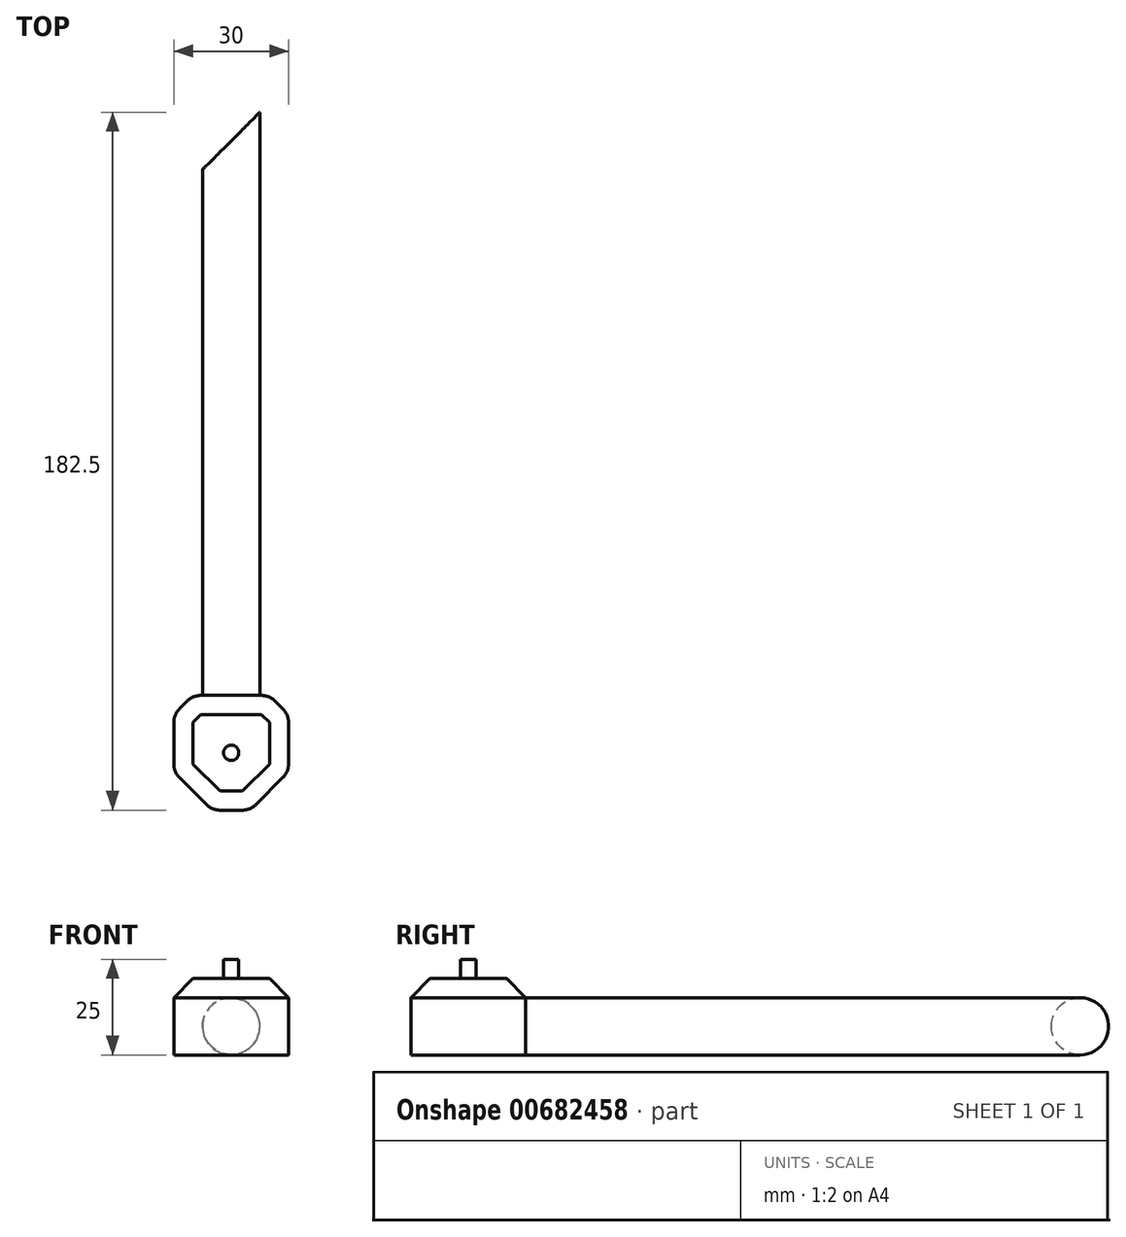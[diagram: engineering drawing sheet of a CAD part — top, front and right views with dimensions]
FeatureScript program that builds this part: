
annotation { "Feature Type Name" : "Feature", "Feature Type Description" : "" }
export const myFeature = defineFeature(function(context is Context, id is Id, definition is map)
    precondition{}
    {
        {
            var Q0;
            Q0=qCreatedBy(makeId("Top.planeOp"),FACE);
            var sketch = newSketch(context, id + "F0", { "sketchPlane" : qUnion([Q0])});
            skLineSegment(sketch, "E0", {"start": v(0, 12.5) * mm, "end": v(0, 150) * mm});
            skLineSegment(sketch, "E1", {"start": v(0, 150) * mm, "end": v(15, 165) * mm});
            skLineSegment(sketch, "E2", {"start": v(15, 165) * mm, "end": v(15, 12.5) * mm});
            skLineSegment(sketch, "E3", {"start": v(12.5, 0) * mm, "end": v(12.5, 0) * mm});
            skLineSegment(sketch, "E4", {"start": v(43.36, 205.51) * mm, "end": v(-124.44, 37.72) * mm, "construction": true});
            skPoint(sketch, "E5.visualSharp", {"position": v(15, 0) * mm});
            skPoint(sketch, "E6.visualSharp", {"position": v(0, 0) * mm});
            skLineSegment(sketch, "E7", {"start": v(15, 12.5) * mm, "end": v(0, 12.5) * mm});
            skSolve(sketch);
        }
        {
            var Q0;
            Q0=makeQuery(id+"F0.imprint","IMPRINT",FACE,{"disambiguationData":[TD([[makeQuery(id+"F0.imprint","IMPRINT",EDGE,{"derivedFrom":sQuery(id+"F0.wireOp",EDGE,"E0")}),-1.0]])]});
            extrude(context, id + "F1", {"entities" : qUnion([Q0]), "depth" : 15 * mm, "offsetDistance" : 25 * mm});
        }
        {
            var Q0;
            Q0=makeQuery(id+"F1.opExtrude","CAP_EDGE",EDGE,{"disambiguationData":[OSD([sQuery(id+"F0.wireOp",EDGE,"E2")])],"isStart":false});
            var Q1;
            Q1=makeQuery(id+"F1.opExtrude","CAP_EDGE",EDGE,{"disambiguationData":[OSD([sQuery(id+"F0.wireOp",EDGE,"E0")])],"isStart":false});
            var Q2;
            Q2=makeQuery(id+"F1.opExtrude","CAP_EDGE",EDGE,{"disambiguationData":[OSD([sQuery(id+"F0.wireOp",EDGE,"E0")])],"isStart":true});
            var Q3;
            Q3=makeQuery(id+"F1.opExtrude","CAP_EDGE",EDGE,{"disambiguationData":[OSD([sQuery(id+"F0.wireOp",EDGE,"E2")])],"isStart":true});
            fillet(context, id + "F2", {"entities" : qUnion([Q0, Q1, Q2, Q3]), "radius" : 7.5 * mm, "tangentPropagation" : true, "allowEdgeOverflow" : false});
        }
        {
            var Q0;
            Q0=qCreatedBy(makeId("Top.planeOp"),FACE);
            var sketch = newSketch(context, id + "F3", { "sketchPlane" : qUnion([Q0])});
            skLineSegment(sketch, "E8.bottom", {"start": v(22.5, 12.5) * mm, "end": v(-7.5, 12.5) * mm});
            skLineSegment(sketch, "E8.top", {"start": v(22.5, -17.5) * mm, "end": v(-7.5, -17.5) * mm});
            skLineSegment(sketch, "E8.left", {"start": v(22.5, 12.5) * mm, "end": v(22.5, -17.5) * mm});
            skLineSegment(sketch, "E8.right", {"start": v(-7.5, 12.5) * mm, "end": v(-7.5, -17.5) * mm});
            skSolve(sketch);
        }
        {
            var Q0;
            Q0 = qSketchRegion(id + "F3", true);
            extrude(context, id + "F4", {"entities" : qUnion([Q0]), "operationType" : NewBodyOperationType.ADD, "depth" : 20 * mm, "offsetDistance" : 25 * mm});
        }
        {
            var Q0;
            Q0=makeQuery(id+"F4.opExtrude","SWEPT_EDGE",EDGE,{"disambiguationData":[OSD([sQuery(id+"F3.wireOp",EDGE,"E8.top"),sQuery(id+"F3.wireOp",EDGE,"E8.right")])]});
            var Q1;
            Q1=makeQuery(id+"F4.opExtrude","SWEPT_EDGE",EDGE,{"disambiguationData":[OSD([sQuery(id+"F3.wireOp",EDGE,"E8.top"),sQuery(id+"F3.wireOp",EDGE,"E8.left")])]});
            chamfer(context, id + "F5", {"entities" : qUnion([Q0, Q1]), "width" : 10 * mm, "tangentPropagation" : true});
        }
        {
            var Q0;
            Q0=makeQuery(id+"F4.opExtrude","SWEPT_EDGE",EDGE,{"disambiguationData":[OSD([sQuery(id+"F3.wireOp",EDGE,"E8.bottom"),sQuery(id+"F3.wireOp",EDGE,"E8.left")])]});
            var Q1;
            Q1=makeQuery(id+"F4.opExtrude","SWEPT_EDGE",EDGE,{"disambiguationData":[OSD([sQuery(id+"F3.wireOp",EDGE,"E8.bottom"),sQuery(id+"F3.wireOp",EDGE,"E8.right")])]});
            chamfer(context, id + "F6", {"entities" : qUnion([Q0, Q1]), "width" : 5 * mm, "tangentPropagation" : true});
        }
        {
            var Q0;
            {var subQ0=sQuery(id+"F3.wireOp",EDGE,"E8.top");Q0=makeQuery(id+"F5.opChamfer","BLEND_EDGE",EDGE,{"blendedFrom":[makeQuery(id+"F4.opExtrude","SWEPT_EDGE",EDGE,{"disambiguationData":[OSD([subQ0,sQuery(id+"F3.wireOp",EDGE,"E8.left")])]}),makeQuery(id+"F4.opExtrude","SWEPT_FACE",FACE,{"disambiguationData":[OSD([subQ0])]})],"blendedInto":[makeQuery(id+"F4.opExtrude","SWEPT_FACE",FACE,{"disambiguationData":[OSD([subQ0])]})]});}
            var Q1;
            {var subQ0=sQuery(id+"F3.wireOp",EDGE,"E8.top");Q1=makeQuery(id+"F5.opChamfer","BLEND_EDGE",EDGE,{"blendedFrom":[makeQuery(id+"F4.opExtrude","SWEPT_EDGE",EDGE,{"disambiguationData":[OSD([subQ0,sQuery(id+"F3.wireOp",EDGE,"E8.right")])]}),makeQuery(id+"F4.opExtrude","SWEPT_FACE",FACE,{"disambiguationData":[OSD([subQ0])]})],"blendedInto":[makeQuery(id+"F4.opExtrude","SWEPT_FACE",FACE,{"disambiguationData":[OSD([subQ0])]})]});}
            var Q2;
            {var subQ0=sQuery(id+"F3.wireOp",EDGE,"E8.right");Q2=makeQuery(id+"F5.opChamfer","BLEND_EDGE",EDGE,{"blendedFrom":[makeQuery(id+"F4.opExtrude","SWEPT_EDGE",EDGE,{"disambiguationData":[OSD([sQuery(id+"F3.wireOp",EDGE,"E8.top"),subQ0])]}),makeQuery(id+"F4.opExtrude","SWEPT_FACE",FACE,{"disambiguationData":[OSD([subQ0])]})],"blendedInto":[makeQuery(id+"F4.opExtrude","SWEPT_FACE",FACE,{"disambiguationData":[OSD([subQ0])]})]});}
            var Q3;
            {var subQ0=sQuery(id+"F3.wireOp",EDGE,"E8.left");Q3=makeQuery(id+"F5.opChamfer","BLEND_EDGE",EDGE,{"blendedFrom":[makeQuery(id+"F4.opExtrude","SWEPT_EDGE",EDGE,{"disambiguationData":[OSD([sQuery(id+"F3.wireOp",EDGE,"E8.top"),subQ0])]}),makeQuery(id+"F4.opExtrude","SWEPT_FACE",FACE,{"disambiguationData":[OSD([subQ0])]})],"blendedInto":[makeQuery(id+"F4.opExtrude","SWEPT_FACE",FACE,{"disambiguationData":[OSD([subQ0])]})]});}
            var Q4;
            {var subQ0=sQuery(id+"F3.wireOp",EDGE,"E8.left");Q4=makeQuery(id+"F6.opChamfer","BLEND_EDGE",EDGE,{"blendedFrom":[makeQuery(id+"F4.opExtrude","SWEPT_EDGE",EDGE,{"disambiguationData":[OSD([sQuery(id+"F3.wireOp",EDGE,"E8.bottom"),subQ0])]}),makeQuery(id+"F4.opExtrude","SWEPT_FACE",FACE,{"disambiguationData":[OSD([subQ0])]})],"blendedInto":[makeQuery(id+"F4.opExtrude","SWEPT_FACE",FACE,{"disambiguationData":[OSD([subQ0])]})]});}
            var Q5;
            {var subQ0=sQuery(id+"F3.wireOp",EDGE,"E8.bottom");Q5=makeQuery(id+"F6.opChamfer","BLEND_EDGE",EDGE,{"blendedFrom":[makeQuery(id+"F4.opExtrude","SWEPT_EDGE",EDGE,{"disambiguationData":[OSD([subQ0,sQuery(id+"F3.wireOp",EDGE,"E8.left")])]}),makeQuery(id+"F4.opExtrude","SWEPT_FACE",FACE,{"disambiguationData":[OSD([subQ0])]})],"blendedInto":[makeQuery(id+"F4.opExtrude","SWEPT_FACE",FACE,{"disambiguationData":[OSD([subQ0])]})]});}
            var Q6;
            {var subQ0=sQuery(id+"F3.wireOp",EDGE,"E8.bottom");Q6=makeQuery(id+"F6.opChamfer","BLEND_EDGE",EDGE,{"blendedFrom":[makeQuery(id+"F4.opExtrude","SWEPT_EDGE",EDGE,{"disambiguationData":[OSD([subQ0,sQuery(id+"F3.wireOp",EDGE,"E8.right")])]}),makeQuery(id+"F4.opExtrude","SWEPT_FACE",FACE,{"disambiguationData":[OSD([subQ0])]})],"blendedInto":[makeQuery(id+"F4.opExtrude","SWEPT_FACE",FACE,{"disambiguationData":[OSD([subQ0])]})]});}
            var Q7;
            {var subQ0=sQuery(id+"F3.wireOp",EDGE,"E8.right");Q7=makeQuery(id+"F6.opChamfer","BLEND_EDGE",EDGE,{"blendedFrom":[makeQuery(id+"F4.opExtrude","SWEPT_EDGE",EDGE,{"disambiguationData":[OSD([sQuery(id+"F3.wireOp",EDGE,"E8.bottom"),subQ0])]}),makeQuery(id+"F4.opExtrude","SWEPT_FACE",FACE,{"disambiguationData":[OSD([subQ0])]})],"blendedInto":[makeQuery(id+"F4.opExtrude","SWEPT_FACE",FACE,{"disambiguationData":[OSD([subQ0])]})]});}
            fillet(context, id + "F7", {"entities" : qUnion([Q0, Q1, Q2, Q3, Q4, Q5, Q6, Q7]), "radius" : 5 * mm, "tangentPropagation" : true, "allowEdgeOverflow" : false});
        }
        {
            var Q0;
            Q0=makeQuery(id+"F4.opExtrude","CAP_FACE",FACE,{"disambiguationData":[OSD([sQuery(id+"F3.wireOp",EDGE,"E8.bottom"),sQuery(id+"F3.wireOp",EDGE,"E8.top"),sQuery(id+"F3.wireOp",EDGE,"E8.left"),sQuery(id+"F3.wireOp",EDGE,"E8.right")])],"isStart":false});
            chamfer(context, id + "F8", {"entities" : qUnion([Q0]), "width" : 5 * mm, "tangentPropagation" : true});
        }
        {
            var Q0;
            Q0=makeQuery(id+"F4.opExtrude","CAP_FACE",FACE,{"disambiguationData":[OSD([sQuery(id+"F3.wireOp",EDGE,"E8.bottom"),sQuery(id+"F3.wireOp",EDGE,"E8.top"),sQuery(id+"F3.wireOp",EDGE,"E8.left"),sQuery(id+"F3.wireOp",EDGE,"E8.right")])],"isStart":false});
            var sketch = newSketch(context, id + "F9", { "sketchPlane" : qUnion([Q0])});
            skCircle(sketch, "E9", {"center": v(7.5, -2.5) * mm, "radius": 2 * mm});
            skPoint(sketch, "E9.centerSnap0", {"position": v(7.5, -12.5) * mm});
            skSolve(sketch);
        }
        {
            var Q0;
            Q0 = qSketchRegion(id + "F9", true);
            extrude(context, id + "F10", {"entities" : qUnion([Q0]), "operationType" : NewBodyOperationType.ADD, "depth" : 5 * mm, "offsetDistance" : 25 * mm});
        }
    });
